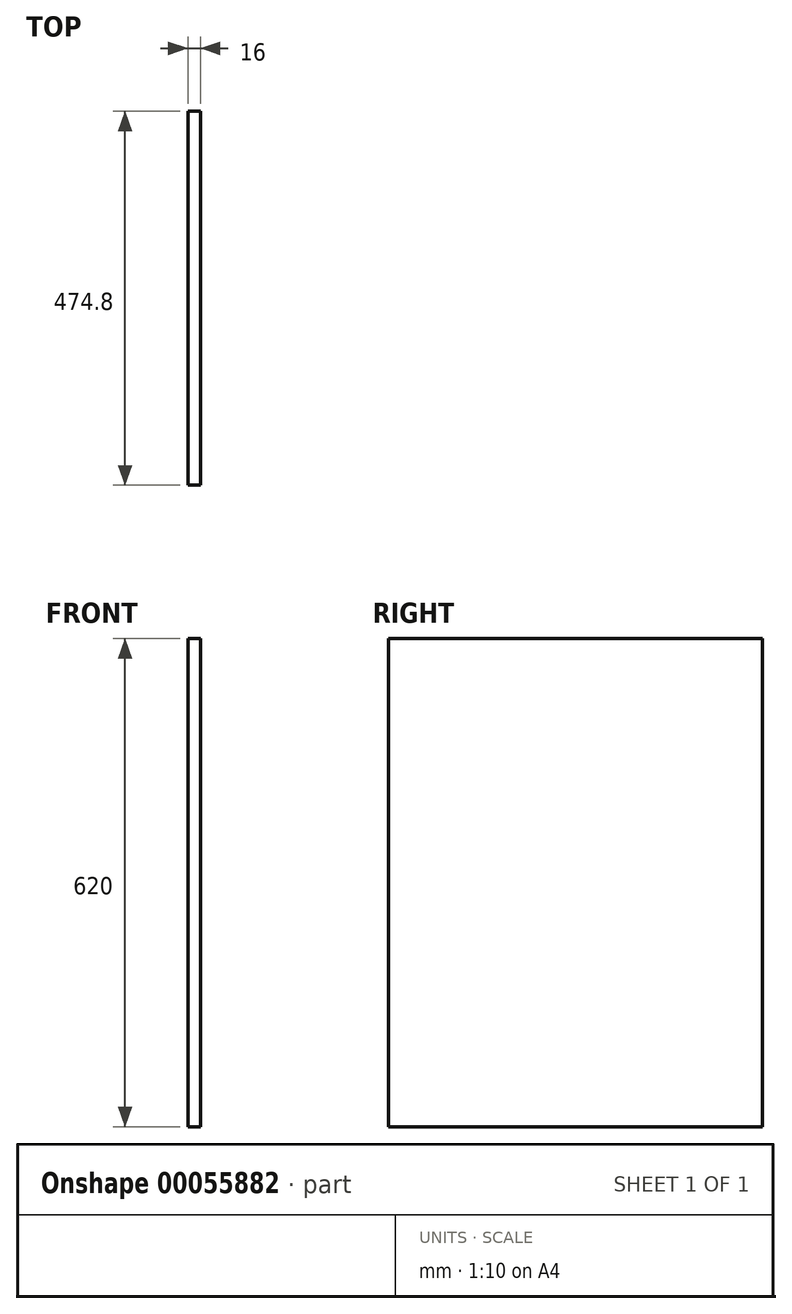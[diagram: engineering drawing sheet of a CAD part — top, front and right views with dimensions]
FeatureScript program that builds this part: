
annotation { "Feature Type Name" : "Feature", "Feature Type Description" : "" }
export const myFeature = defineFeature(function(context is Context, id is Id, definition is map)
    precondition{}
    {
        {
            var Q0;
            Q0=qCreatedBy(makeId("Front.planeOp"),FACE);
            var sketch = newSketch(context, id + "F0", { "sketchPlane" : qUnion([Q0])});
            skLineSegment(sketch, "E0.rect.bottom", {"start": v(-8, 310) * mm, "end": v(8, 310) * mm});
            skLineSegment(sketch, "E0.rect.top", {"start": v(-8, -310) * mm, "end": v(8, -310) * mm});
            skLineSegment(sketch, "E0.rect.left", {"start": v(-8, 310) * mm, "end": v(-8, -310) * mm});
            skLineSegment(sketch, "E0.rect.right", {"start": v(8, 310) * mm, "end": v(8, -310) * mm});
            skPoint(sketch, "E0.rect.middle", {"position": v(0, 0) * mm});
            skSolve(sketch);
        }
        {
            var Q0;
            Q0=makeQuery(id+"F0.imprint","IMPRINT",FACE,{"disambiguationData":[TD([[makeQuery(id+"F0.imprint","IMPRINT",EDGE,{"derivedFrom":sQuery(id+"F0.wireOp",EDGE,"E0.rect.bottom")}),-1.0]])]});
            extrude(context, id + "F1", {"entities" : qUnion([Q0]), "oppositeDirection" : true, "depth" : 474.8 * mm});
        }
    });
